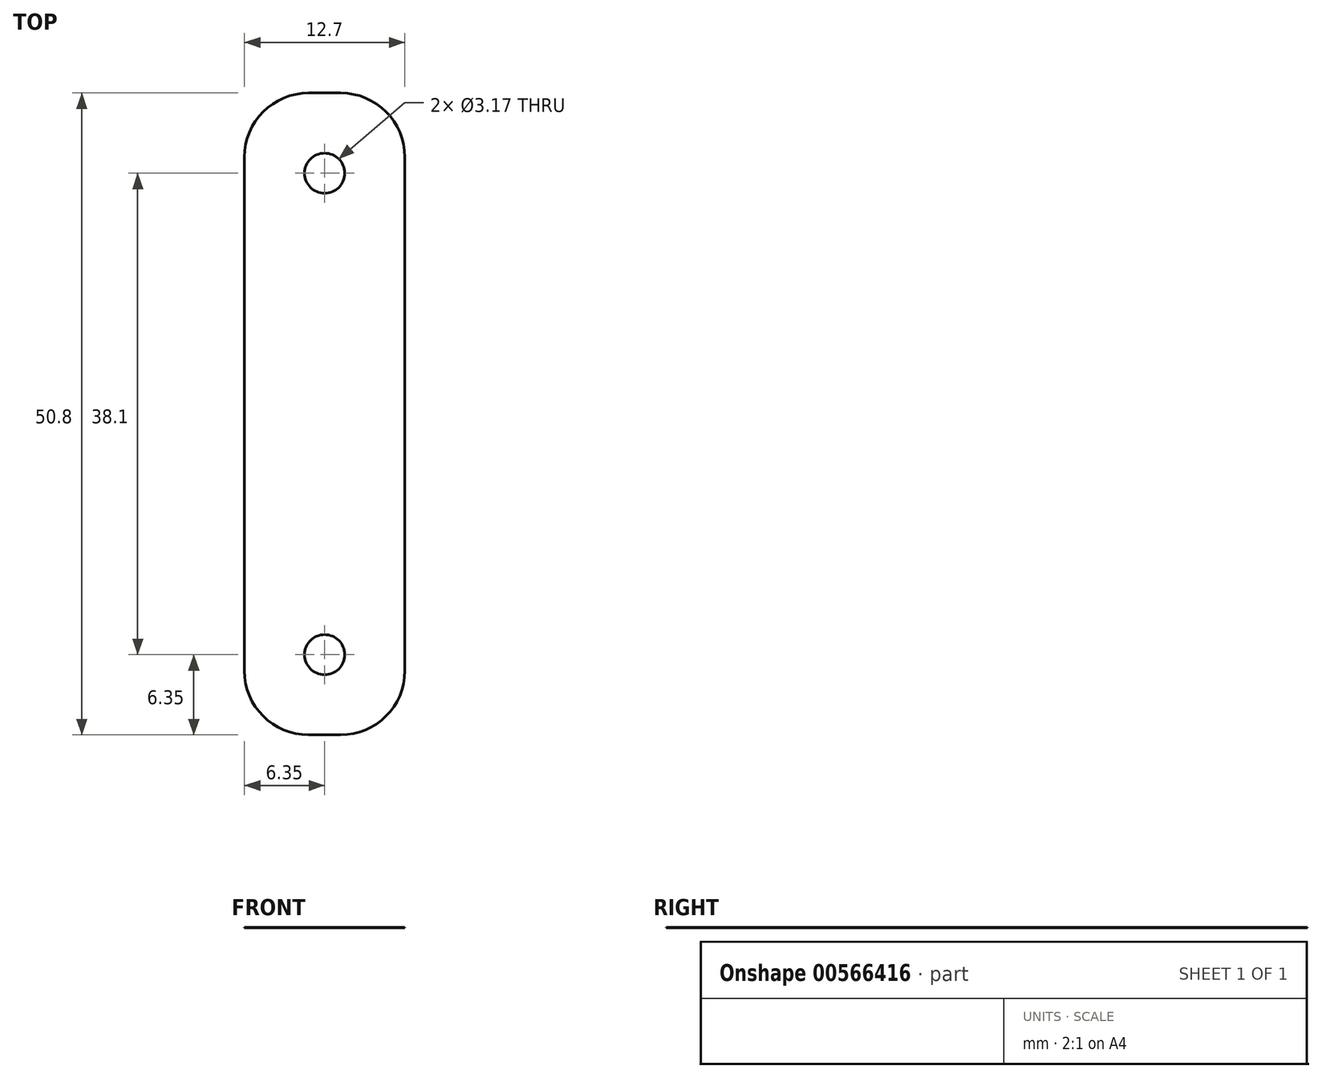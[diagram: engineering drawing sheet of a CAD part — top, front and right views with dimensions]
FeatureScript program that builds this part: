
annotation { "Feature Type Name" : "Feature", "Feature Type Description" : "" }
export const myFeature = defineFeature(function(context is Context, id is Id, definition is map)
    precondition{}
    {
        {
            var Q0;
            Q0=qCreatedBy(makeId("Top.planeOp"),FACE);
            var sketch = newSketch(context, id + "F0", { "sketchPlane" : qUnion([Q0])});
            skLineSegment(sketch, "E0.bottom", {"start": v(0, 0) * mm, "end": v(12.7, 0) * mm});
            skLineSegment(sketch, "E0.top", {"start": v(0, 50.8) * mm, "end": v(12.7, 50.8) * mm});
            skLineSegment(sketch, "E0.left", {"start": v(0, 0) * mm, "end": v(0, 50.8) * mm});
            skLineSegment(sketch, "E0.right", {"start": v(12.7, 0) * mm, "end": v(12.7, 50.8) * mm});
            skCircle(sketch, "E1", {"center": v(6.35, 6.35) * mm, "radius": 1.59 * mm});
            skLineSegment(sketch, "E2", {"start": v(0, 6.35) * mm, "end": v(12.7, 6.35) * mm, "construction": true});
            skLineSegment(sketch, "E3", {"start": v(12.7, 25.4) * mm, "end": v(0, 25.4) * mm, "construction": true});
            skCircle(sketch, "E4.MirrorC", {"center": v(6.35, 44.45) * mm, "radius": 1.59 * mm});
            skSolve(sketch);
        }
        {
            var Q0;
            Q0=makeQuery(id+"F0.imprint","IMPRINT",FACE,{"disambiguationData":[TD([[makeQuery(id+"F0.imprint","IMPRINT",EDGE,{"derivedFrom":sQuery(id+"F0.wireOp",EDGE,"E0.bottom")}),1.0]])]});
            extrude(context, id + "F1", {"entities" : qUnion([Q0]), "depth" : 1 / 203.2 * mm, "offsetDistance" : 25.4 * mm});
        }
        {
            var Q0;
            Q0=makeQuery(id+"F1.opExtrude","SWEPT_EDGE",EDGE,{"disambiguationData":[OSD([sQuery(id+"F0.wireOp",EDGE,"E0.bottom"),sQuery(id+"F0.wireOp",EDGE,"E0.right")])]});
            var Q1;
            Q1=makeQuery(id+"F1.opExtrude","SWEPT_EDGE",EDGE,{"disambiguationData":[OSD([sQuery(id+"F0.wireOp",EDGE,"E0.bottom"),sQuery(id+"F0.wireOp",EDGE,"E0.left")])]});
            var Q2;
            Q2=makeQuery(id+"F1.opExtrude","SWEPT_EDGE",EDGE,{"disambiguationData":[OSD([sQuery(id+"F0.wireOp",EDGE,"E0.top"),sQuery(id+"F0.wireOp",EDGE,"E0.right")])]});
            var Q3;
            Q3=makeQuery(id+"F1.opExtrude","SWEPT_EDGE",EDGE,{"disambiguationData":[OSD([sQuery(id+"F0.wireOp",EDGE,"E0.top"),sQuery(id+"F0.wireOp",EDGE,"E0.left")])]});
            fillet(context, id + "F2", {"entities" : qUnion([Q0, Q1, Q2, Q3]), "radius" : 5.08 * mm, "tangentPropagation" : true, "allowEdgeOverflow" : false});
        }
    });
